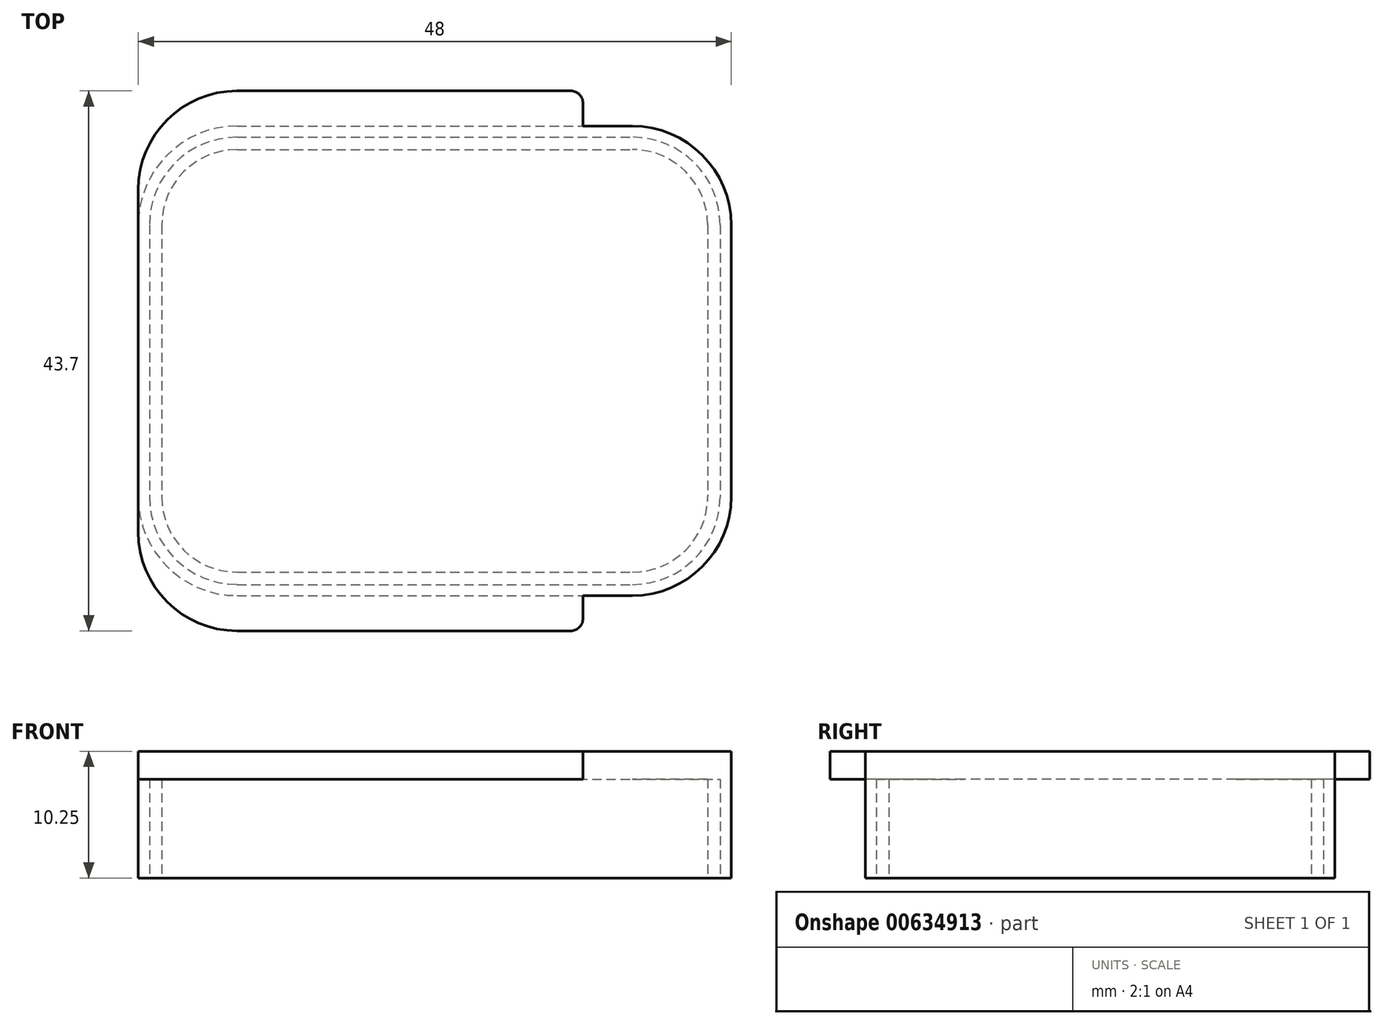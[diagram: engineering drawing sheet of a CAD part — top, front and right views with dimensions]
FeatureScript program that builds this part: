
annotation { "Feature Type Name" : "Feature", "Feature Type Description" : "" }
export const myFeature = defineFeature(function(context is Context, id is Id, definition is map)
    precondition{}
    {
        {
            var Q0;
            Q0=qCreatedBy(makeId("Top.planeOp"),FACE);
            var sketch = newSketch(context, id + "F0", { "sketchPlane" : qUnion([Q0])});
            skLineSegment(sketch, "E0.bottom", {"start": v(-16, 19) * mm, "end": v(16, 19) * mm});
            skLineSegment(sketch, "E0.top", {"start": v(-16, -19) * mm, "end": v(16, -19) * mm});
            skLineSegment(sketch, "E0.left", {"start": v(-24, 11) * mm, "end": v(-24, -11) * mm});
            skLineSegment(sketch, "E0.right", {"start": v(24, 11) * mm, "end": v(24, -11) * mm});
            skPoint(sketch, "E1.visualSharp", {"position": v(-24, 19) * mm});
            skArc(sketch, "E1.filletArc", {"start": v(-16, 19) * mm, "mid": v(-21.66, 16.66) * mm, "end": v(-24, 11) * mm});
            skPoint(sketch, "E2.visualSharp", {"position": v(24, 19) * mm});
            skArc(sketch, "E2.filletArc", {"start": v(24, 11) * mm, "mid": v(21.66, 16.66) * mm, "end": v(16, 19) * mm});
            skPoint(sketch, "E3.visualSharp", {"position": v(24, -19) * mm});
            skArc(sketch, "E3.filletArc", {"start": v(16, -19) * mm, "mid": v(21.66, -16.66) * mm, "end": v(24, -11) * mm});
            skPoint(sketch, "E4.visualSharp", {"position": v(-24, -19) * mm});
            skArc(sketch, "E4.filletArc", {"start": v(-24, -11) * mm, "mid": v(-21.66, -16.66) * mm, "end": v(-16, -19) * mm});
            skSolve(sketch);
        }
        {
            var Q0;
            Q0=makeQuery(id+"F0.imprint","IMPRINT",FACE,{"disambiguationData":[TD([[makeQuery(id+"F0.imprint","IMPRINT",EDGE,{"derivedFrom":sQuery(id+"F0.wireOp",EDGE,"E0.bottom")}),-1.0]])]});
            extrude(context, id + "F1", {"entities" : qUnion([Q0]), "depth" : 10.25 * mm, "offsetDistance" : 25 * mm});
        }
        {
            var Q0;
            Q0=makeQuery(id+"F1.opExtrude","CAP_FACE",FACE,{"disambiguationData":[OSD([sQuery(id+"F0.wireOp",EDGE,"E0.bottom"),sQuery(id+"F0.wireOp",EDGE,"E0.top"),sQuery(id+"F0.wireOp",EDGE,"E0.left"),sQuery(id+"F0.wireOp",EDGE,"E0.right"),sQuery(id+"F0.wireOp",EDGE,"E1.filletArc"),sQuery(id+"F0.wireOp",EDGE,"E2.filletArc"),sQuery(id+"F0.wireOp",EDGE,"E3.filletArc"),sQuery(id+"F0.wireOp",EDGE,"E4.filletArc")])],"isStart":false});
            var sketch = newSketch(context, id + "F2", { "sketchPlane" : qUnion([Q0])});
            skLineSegment(sketch, "E5.bottom", {"start": v(-16, 21.85) * mm, "end": v(12, 21.85) * mm});
            skLineSegment(sketch, "E5.top", {"start": v(-16, -21.85) * mm, "end": v(12, -21.85) * mm});
            skLineSegment(sketch, "E5.left", {"start": v(-24, 13.85) * mm, "end": v(-24, -13.85) * mm});
            skLineSegment(sketch, "E5.right", {"start": v(12, 21.85) * mm, "end": v(12, -21.85) * mm});
            skPoint(sketch, "E6.visualSharp", {"position": v(-24, 21.85) * mm});
            skArc(sketch, "E6.filletArc", {"start": v(-16, 21.85) * mm, "mid": v(-21.66, 19.5) * mm, "end": v(-24, 13.85) * mm});
            skPoint(sketch, "E7.visualSharp", {"position": v(-24, -21.85) * mm});
            skArc(sketch, "E7.filletArc", {"start": v(-24, -13.85) * mm, "mid": v(-21.66, -19.5) * mm, "end": v(-16, -21.85) * mm});
            skSolve(sketch);
        }
        {
            var Q0;
            {var subQ4=sQuery(id+"F2.wireOp",EDGE,"E5.bottom");Q0=makeQuery(id+"F2.imprint","IMPRINT",FACE,{"disambiguationData":[TD([[makeQuery(id+"F2.imprint","IMPRINT",EDGE,{"derivedFrom":subQ4}),-1.0]])]});}
            var Q1;
            {var subQ1=sQuery(id+"F2.wireOp",EDGE,"E5.top");Q1=makeQuery(id+"F2.imprint","IMPRINT",FACE,{"disambiguationData":[TD([[makeQuery(id+"F2.imprint","IMPRINT",EDGE,{"derivedFrom":subQ1}),1.0]])]});}
            extrude(context, id + "F3", {"entities" : qUnion([Q0, Q1]), "operationType" : NewBodyOperationType.ADD, "oppositeDirection" : true, "depth" : 2.25 * mm, "offsetDistance" : 25 * mm});
        }
        {
            var Q0;
            Q0=makeQuery(id+"F3.opExtrude","SWEPT_EDGE",EDGE,{"disambiguationData":[OSD([sQuery(id+"F0.wireOp",EDGE,"E0.top"),sQuery(id+"F2.wireOp",EDGE,"E5.right")])]});
            var Q1;
            Q1=makeQuery(id+"F3.opExtrude","SWEPT_EDGE",EDGE,{"disambiguationData":[OSD([sQuery(id+"F2.wireOp",EDGE,"E5.top"),sQuery(id+"F2.wireOp",EDGE,"E5.right")])]});
            var Q2;
            Q2=makeQuery(id+"F3.opExtrude","SWEPT_EDGE",EDGE,{"disambiguationData":[OSD([sQuery(id+"F2.wireOp",EDGE,"E5.bottom"),sQuery(id+"F2.wireOp",EDGE,"E5.right")])]});
            var Q3;
            Q3=makeQuery(id+"F3.opExtrude","SWEPT_EDGE",EDGE,{"disambiguationData":[OSD([sQuery(id+"F0.wireOp",EDGE,"E0.bottom"),sQuery(id+"F2.wireOp",EDGE,"E5.right")])]});
            fillet(context, id + "F4", {"entities" : qUnion([Q0, Q1, Q2, Q3]), "radius" : 1 * mm, "tangentPropagation" : true, "allowEdgeOverflow" : false});
        }
        {
            var Q0;
            Q0=makeQuery(id+"F1.opExtrude","CAP_FACE",FACE,{"disambiguationData":[OSD([sQuery(id+"F0.wireOp",EDGE,"E0.bottom"),sQuery(id+"F0.wireOp",EDGE,"E0.top"),sQuery(id+"F0.wireOp",EDGE,"E0.left"),sQuery(id+"F0.wireOp",EDGE,"E0.right"),sQuery(id+"F0.wireOp",EDGE,"E1.filletArc"),sQuery(id+"F0.wireOp",EDGE,"E2.filletArc"),sQuery(id+"F0.wireOp",EDGE,"E3.filletArc"),sQuery(id+"F0.wireOp",EDGE,"E4.filletArc")])],"isStart":true});
            var sketch = newSketch(context, id + "F5", { "sketchPlane" : qUnion([Q0])});
            skPoint(sketch, "E8.visualSharp", {"position": v(-22.6, 17.1) * mm});
            skPoint(sketch, "E9.visualSharp", {"position": v(22.6, 17.1) * mm});
            skPoint(sketch, "E10.visualSharp", {"position": v(22.6, -17.1) * mm});
            skPoint(sketch, "E11.visualSharp", {"position": v(-22.6, -17.1) * mm});
            skLineSegment(sketch, "E12.0", {"start": v(-16, 18.1) * mm, "end": v(16, 18.1) * mm});
            skArc(sketch, "E13.0", {"start": v(16, 18.1) * mm, "mid": v(21.02, 16.02) * mm, "end": v(23.1, 11) * mm});
            skLineSegment(sketch, "E14.0", {"start": v(23.1, -11) * mm, "end": v(23.1, 11) * mm});
            skArc(sketch, "E15.0", {"start": v(23.1, -11) * mm, "mid": v(21.02, -16.02) * mm, "end": v(16, -18.1) * mm});
            skLineSegment(sketch, "E16.0", {"start": v(-16, -18.1) * mm, "end": v(16, -18.1) * mm});
            skArc(sketch, "E17.0", {"start": v(-16, -18.1) * mm, "mid": v(-21.02, -16.02) * mm, "end": v(-23.1, -11) * mm});
            skLineSegment(sketch, "E18.0", {"start": v(-23.1, -11) * mm, "end": v(-23.1, 11) * mm});
            skArc(sketch, "E19.0", {"start": v(-23.1, 11) * mm, "mid": v(-21.02, 16.02) * mm, "end": v(-16, 18.1) * mm});
            skArc(sketch, "E20.0", {"start": v(-22.1, 11) * mm, "mid": v(-20.31, 15.31) * mm, "end": v(-16, 17.1) * mm});
            skLineSegment(sketch, "E21.0", {"start": v(-16, 17.1) * mm, "end": v(16, 17.1) * mm});
            skArc(sketch, "E22.0", {"start": v(16, 17.1) * mm, "mid": v(20.31, 15.31) * mm, "end": v(22.1, 11) * mm});
            skLineSegment(sketch, "E23.0", {"start": v(22.1, -11) * mm, "end": v(22.1, 11) * mm});
            skArc(sketch, "E24.0", {"start": v(22.1, -11) * mm, "mid": v(20.31, -15.31) * mm, "end": v(16, -17.1) * mm});
            skLineSegment(sketch, "E25.0", {"start": v(-16, -17.1) * mm, "end": v(16, -17.1) * mm});
            skArc(sketch, "E26.0", {"start": v(-16, -17.1) * mm, "mid": v(-20.31, -15.31) * mm, "end": v(-22.1, -11) * mm});
            skLineSegment(sketch, "E27.0", {"start": v(-22.1, -11) * mm, "end": v(-22.1, 11) * mm});
            skSolve(sketch);
        }
        {
            var Q0;
            Q0=makeQuery(id+"F5.imprint","IMPRINT",FACE,{"disambiguationData":[TD([[makeQuery(id+"F5.imprint","IMPRINT",EDGE,{"derivedFrom":sQuery(id+"F5.wireOp",EDGE,"E20.0")}),-1.0]])]});
            extrude(context, id + "F6", {"entities" : qUnion([Q0]), "operationType" : NewBodyOperationType.REMOVE, "oppositeDirection" : true, "depth" : 8 * mm, "offsetDistance" : 25 * mm});
        }
        {
            var Q0;
            Q0=makeQuery(id+"F5.imprint","IMPRINT",FACE,{"disambiguationData":[TD([[makeQuery(id+"F5.imprint","IMPRINT",EDGE,{"derivedFrom":sQuery(id+"F5.wireOp",EDGE,"E12.0")}),-1.0]])]});
            extrude(context, id + "F7", {"entities" : qUnion([Q0]), "operationType" : NewBodyOperationType.REMOVE, "oppositeDirection" : true, "depth" : 2.5 * mm, "offsetDistance" : 25 * mm});
        }
    });
